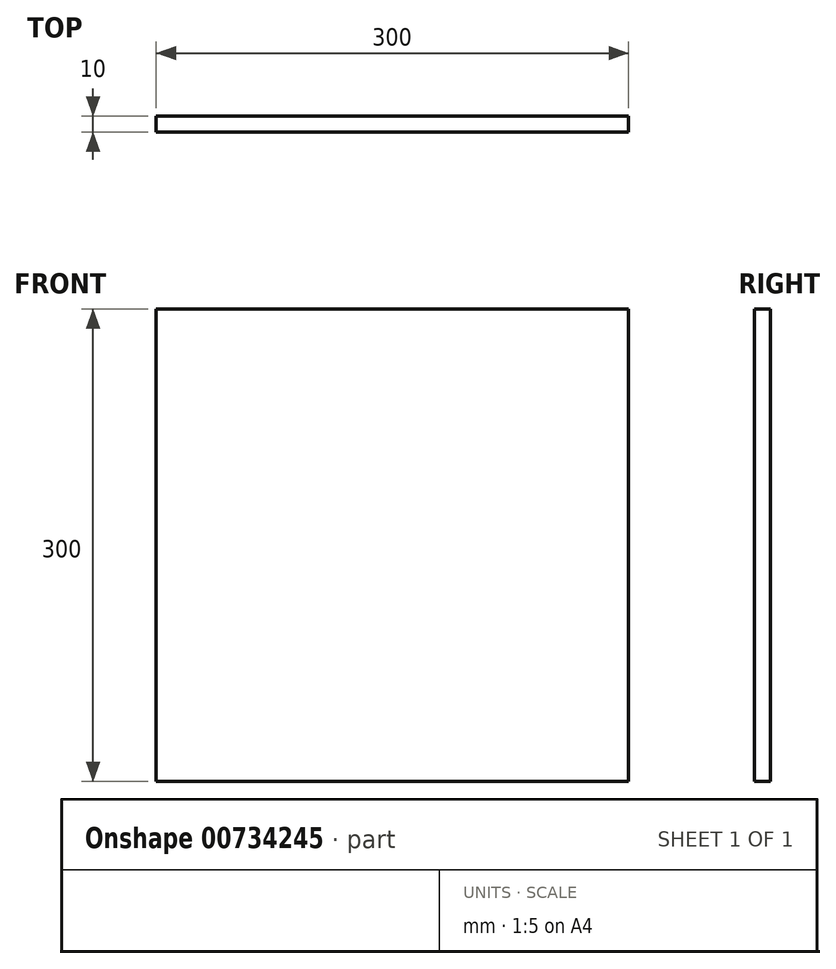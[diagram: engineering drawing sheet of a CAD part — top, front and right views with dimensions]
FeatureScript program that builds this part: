
annotation { "Feature Type Name" : "Feature", "Feature Type Description" : "" }
export const myFeature = defineFeature(function(context is Context, id is Id, definition is map)
    precondition{}
    {
        {
            var Q0;
            Q0=qCreatedBy(makeId("Front.planeOp"),FACE);
            var sketch = newSketch(context, id + "F0", { "sketchPlane" : qUnion([Q0])});
            skLineSegment(sketch, "E0.bottom", {"start": v(150, 150) * mm, "end": v(-150, 150) * mm});
            skLineSegment(sketch, "E0.top", {"start": v(150, -150) * mm, "end": v(-150, -150) * mm});
            skLineSegment(sketch, "E0.left", {"start": v(150, 150) * mm, "end": v(150, -150) * mm});
            skLineSegment(sketch, "E0.right", {"start": v(-150, 150) * mm, "end": v(-150, -150) * mm});
            skPoint(sketch, "E0.middle", {"position": v(0, 0) * mm});
            skSolve(sketch);
        }
        {
            var Q0;
            Q0=qSketchRegion(id+"F0",true);
            extrude(context, id + "F1", {"entities" : qUnion([Q0]), "depth" : 10 * mm, "offsetDistance" : 25 * mm});
        }
    });
